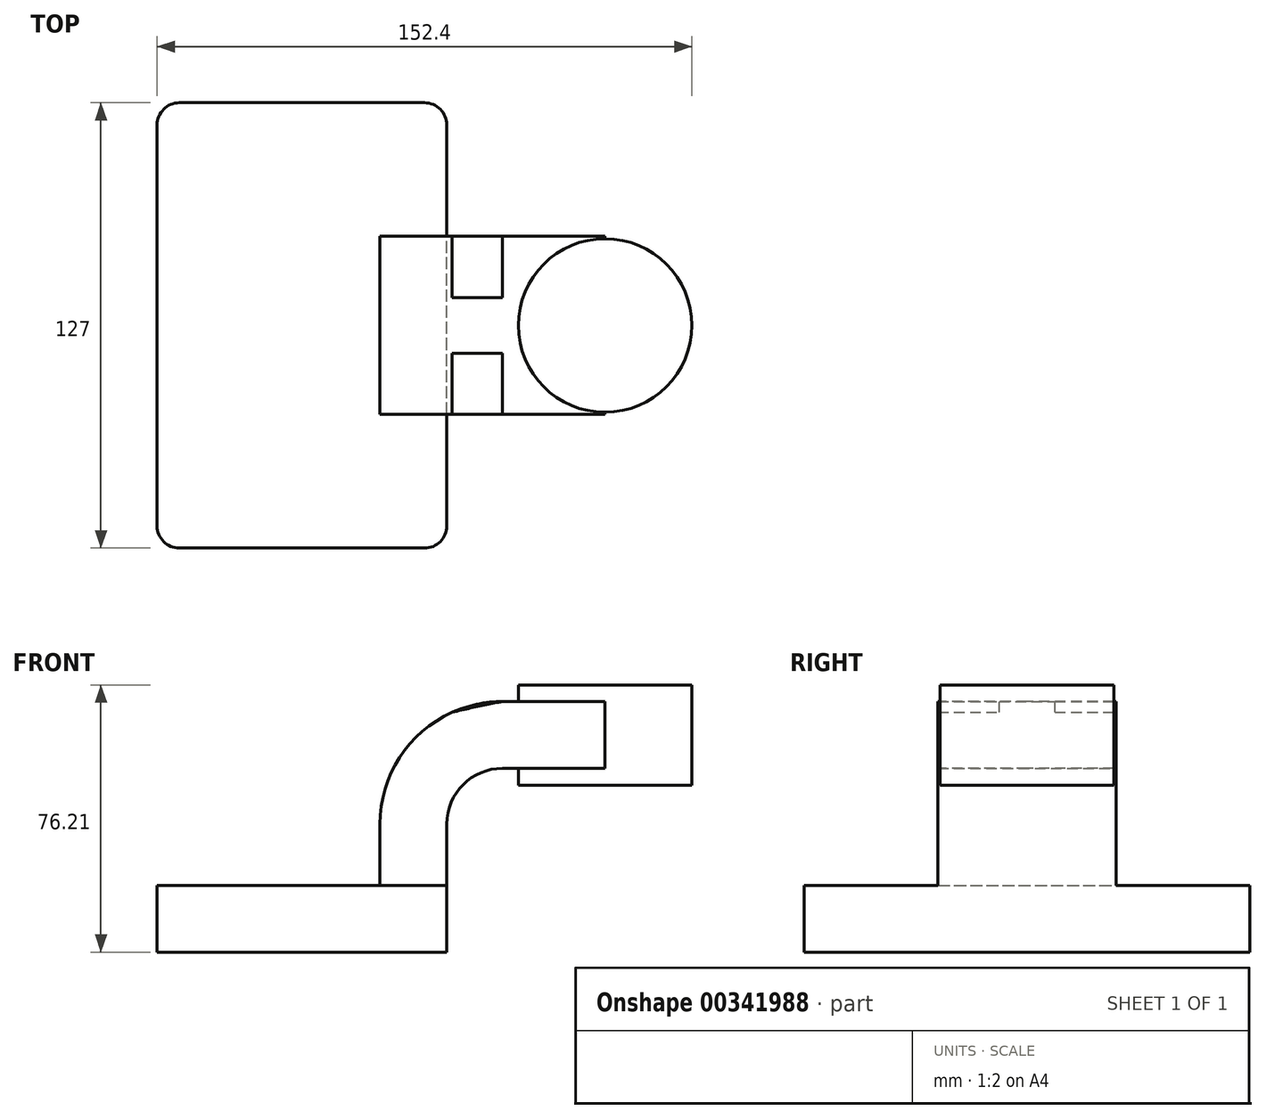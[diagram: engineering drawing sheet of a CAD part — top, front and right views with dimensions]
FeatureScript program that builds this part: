
annotation { "Feature Type Name" : "Feature", "Feature Type Description" : "" }
export const myFeature = defineFeature(function(context is Context, id is Id, definition is map)
    precondition{}
    {
        {
            var Q0;
            Q0=qCreatedBy(makeId("Front.planeOp"),FACE);
            var sketch = newSketch(context, id + "F0", { "sketchPlane" : qUnion([Q0])});
            skLineSegment(sketch, "E0.bottom", {"start": v(41.28, -9.52) * mm, "end": v(-41.28, -9.53) * mm});
            skLineSegment(sketch, "E0.top", {"start": v(41.27, 9.53) * mm, "end": v(-41.28, 9.53) * mm});
            skLineSegment(sketch, "E0.left", {"start": v(41.28, -9.52) * mm, "end": v(41.28, 9.53) * mm});
            skLineSegment(sketch, "E0.right", {"start": v(-41.28, -9.53) * mm, "end": v(-41.28, 9.53) * mm});
            skPoint(sketch, "E0.middle", {"position": v(0, 0) * mm});
            skLineSegment(sketch, "E1.bottom", {"start": v(111.12, 38.1) * mm, "end": v(60.32, 38.1) * mm});
            skLineSegment(sketch, "E1.top", {"start": v(111.12, 66.68) * mm, "end": v(60.32, 66.68) * mm});
            skLineSegment(sketch, "E1.left", {"start": v(111.12, 38.1) * mm, "end": v(111.12, 66.68) * mm});
            skLineSegment(sketch, "E1.right", {"start": v(60.32, 38.1) * mm, "end": v(60.32, 66.68) * mm});
            skPoint(sketch, "E1.middle", {"position": v(85.72, 52.39) * mm});
            skLineSegment(sketch, "E2", {"start": v(41.27, 9.53) * mm, "end": v(41.27, 27) * mm});
            skArc(sketch, "E3", {"start": v(41.27, 27) * mm, "mid": v(45.92, 38.23) * mm, "end": v(57.15, 42.88) * mm});
            skLineSegment(sketch, "E4", {"start": v(57.15, 42.88) * mm, "end": v(86.38, 42.88) * mm});
            skLineSegment(sketch, "E5.0", {"start": v(57.15, 61.93) * mm, "end": v(86.38, 61.93) * mm});
            skArc(sketch, "E5.1", {"start": v(22.23, 27) * mm, "mid": v(32.45, 51.7) * mm, "end": v(57.15, 61.93) * mm});
            skLineSegment(sketch, "E5.2", {"start": v(22.22, 9.53) * mm, "end": v(22.22, 27) * mm});
            skLineSegment(sketch, "E6", {"start": v(86.38, 38.1) * mm, "end": v(86.38, 66.68) * mm});
            skFitSpline(sketch, "E7", {"points": [v(-41.28, 9.53) * mm, v(57.15, 61.93) * mm], "startDerivative": vector(61.56, 98.85) * mm, "endDerivative": vector(77.97, 14.12) * mm});
            skSolve(sketch);
        }
        {
            var Q0;
            Q0=makeQuery(id+"F0.imprint","IMPRINT",FACE,{"disambiguationData":[TD([[makeQuery(id+"F0.imprint","IMPRINT",EDGE,{"derivedFrom":sQuery(id+"F0.wireOp",EDGE,"E0.bottom")}),-1.0]])]});
            extrude(context, id + "F1", {"entities" : qUnion([Q0]), "endBound" : BoundingType.SYMMETRIC, "depth" : 127 * mm});
        }
        {
            var Q0;
            {var subQ0=sQuery(id+"F0.wireOp",EDGE,"E4");var subQ1=sQuery(id+"F0.wireOp",EDGE,"E1.right");var subQ2=makeQuery(id+"F0.imprint","INTERSECT",VERTEX,{"derivedFrom":[subQ1,subQ0]});Q0=makeQuery(id+"F0.imprint","IMPRINT",FACE,{"disambiguationData":[TD([[makeQuery(id+"F0.imprint","IMPRINT",EDGE,{"disambiguationData":[TD([[subQ2,-1.0]])],"derivedFrom":subQ1}),-1.0]])]});}
            var Q1;
            {var subQ1=sQuery(id+"F0.wireOp",EDGE,"E2");Q1=makeQuery(id+"F0.imprint","IMPRINT",FACE,{"disambiguationData":[TD([[makeQuery(id+"F0.imprint","IMPRINT",EDGE,{"derivedFrom":subQ1}),1.0]])]});}
            extrude(context, id + "F2", {"entities" : qUnion([Q0, Q1]), "operationType" : NewBodyOperationType.ADD, "endBound" : BoundingType.SYMMETRIC, "depth" : 50.8 * mm});
        }
        {
            var Q0;
            Q0=makeQuery(id+"F0.imprint","IMPRINT",FACE,{"disambiguationData":[TD([[makeQuery(id+"F0.imprint","IMPRINT",EDGE,{"derivedFrom":sQuery(id+"F0.wireOp",EDGE,"E5.1")}),1.0]])]});
            extrude(context, id + "F3", {"entities" : qUnion([Q0]), "operationType" : NewBodyOperationType.ADD, "endBound" : BoundingType.SYMMETRIC, "depth" : 15.88 * mm});
        }
        {
            var Q0;
            {var subQ0=sQuery(id+"F0.wireOp",EDGE,"E1.left");Q0=makeQuery(id+"F0.imprint","IMPRINT",FACE,{"disambiguationData":[TD([[makeQuery(id+"F0.imprint","IMPRINT",EDGE,{"derivedFrom":subQ0}),1.0]])]});}
            var Q1;
            Q1=sQuery(id+"F0.wireOp",EDGE,"E6");
            revolve(context, id + "F4", {"operationType" : NewBodyOperationType.ADD, "entities" : qUnion([Q0]), "axis" : qUnion([Q1]), "revolveType" : RevolveType.FULL});
        }
        {
            var Q0;
            Q0=makeQuery(id+"F1.opExtrude","CAP_EDGE",EDGE,{"disambiguationData":[OSD([sQuery(id+"F0.wireOp",EDGE,"E0.left")])],"isStart":false});
            var Q1;
            Q1=makeQuery(id+"F1.opExtrude","CAP_EDGE",EDGE,{"disambiguationData":[OSD([sQuery(id+"F0.wireOp",EDGE,"E0.right")])],"isStart":false});
            var Q2;
            Q2=makeQuery(id+"F1.opExtrude","CAP_EDGE",EDGE,{"disambiguationData":[OSD([sQuery(id+"F0.wireOp",EDGE,"E0.right")])],"isStart":true});
            var Q3;
            Q3=makeQuery(id+"F1.opExtrude","CAP_EDGE",EDGE,{"disambiguationData":[OSD([sQuery(id+"F0.wireOp",EDGE,"E0.left")])],"isStart":true});
            fillet(context, id + "F5", {"entities" : qUnion([Q0, Q1, Q2, Q3]), "radius" : 6.35 * mm, "tangentPropagation" : true, "allowEdgeOverflow" : false});
        }
    });
